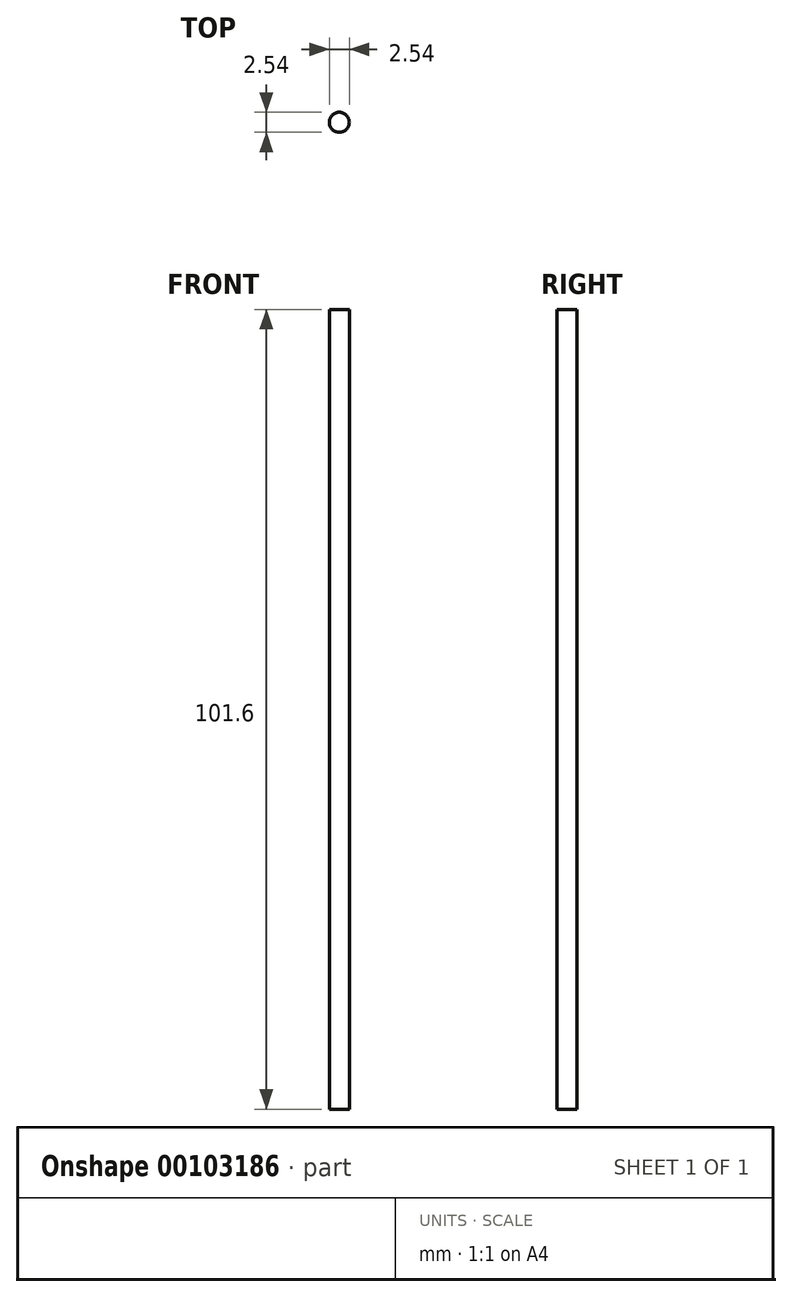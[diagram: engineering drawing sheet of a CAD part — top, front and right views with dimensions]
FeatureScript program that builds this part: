
annotation { "Feature Type Name" : "Feature", "Feature Type Description" : "" }
export const myFeature = defineFeature(function(context is Context, id is Id, definition is map)
    precondition{}
    {
        {
            var Q0;
            Q0=qCreatedBy(makeId("Top.planeOp"),FACE);
            var sketch = newSketch(context, id + "F0", { "sketchPlane" : qUnion([Q0])});
            skCircle(sketch, "E0", {"center": v(0, 0) * mm, "radius": 1.27 * mm});
            skSolve(sketch);
        }
        {
            var Q0;
            Q0=makeQuery(id+"F0.imprint","IMPRINT",FACE,{"disambiguationData":[TD([[makeQuery(id+"F0.imprint","IMPRINT",EDGE,{"derivedFrom":sQuery(id+"F0.wireOp",EDGE,"E0")}),1.0]])]});
            extrude(context, id + "F1", {"entities" : qUnion([Q0]), "endBound" : BoundingType.SYMMETRIC, "depth" : 101.6 * mm});
        }
    });
